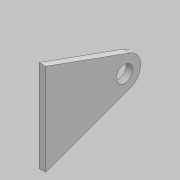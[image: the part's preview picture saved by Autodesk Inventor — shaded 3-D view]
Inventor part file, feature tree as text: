
AUTODESK INVENTOR PART (.ipt)
format: ipt  version: 2018 (Build 220112000, 112)  size: 80,384 bytes
history: native  units: mm
features: other x1, extrude x1, sketch x1
ambient origin geometry x8: Origin, YZ Plane, XZ Plane, XY Plane, X Axis, Y Axis, Z Axis, Center Point
bodies: Body1 (feature_tree)
feature tree (3):
  other  "實體1"
  extrude  "擠出1"  Depth=50.0mm
  sketch  "草圖1"
